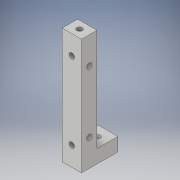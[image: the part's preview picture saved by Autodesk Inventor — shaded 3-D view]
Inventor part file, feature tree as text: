
AUTODESK INVENTOR PART (.ipt)
format: ipt  version: 2019 (Build 230136000, 136)  size: 139,264 bytes
history: native  units: mm
features: sketch x6, hole x4, extrude x2, projected_geometry x2, other x1
ambient origin geometry x8: Origin, YZ Plane, XZ Plane, XY Plane, X Axis, Y Axis, Z Axis, Center Point
bodies: Body1 (feature_tree)
feature tree (15):
  other  "Твердое тело1"
  extrude  "Выдавливание1"  Depth=10.0mm
  extrude  "Выдавливание2"  Depth=18.8mm
  hole  "Отверстие1"  [1 undecoded]
  hole  "Отверстие2"  [1 undecoded]
  hole  "Отверстие3"  [1 undecoded]
  hole  "Отверстие4"  [1 undecoded]
  sketch  "Эскиз1"
  sketch  "Эскиз2"
  sketch  "Эскиз4"
  projected_geometry  "Спроецированная петля1"
  projected_geometry  "Спроецированная петля2"
  sketch  "Эскиз7"
  sketch  "Эскиз9"
  sketch  "Эскиз11"
note: 4 required parameter values undecoded (feature->parameter linkage not recoverable at this tier; creation-order binding heuristic only, values carry confidence <= 0.55)
